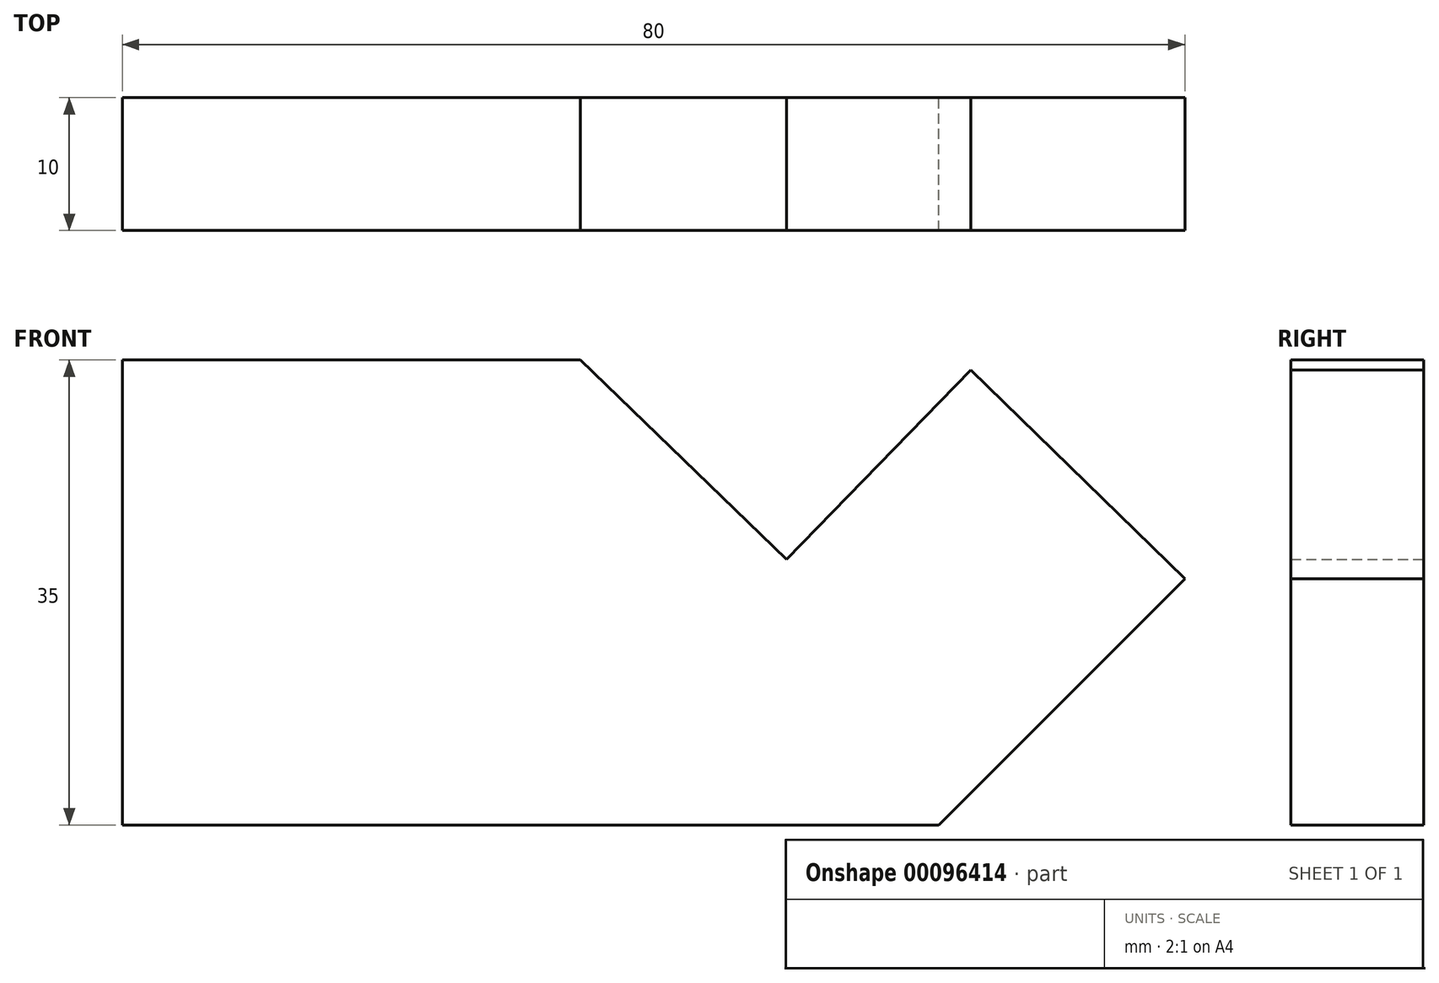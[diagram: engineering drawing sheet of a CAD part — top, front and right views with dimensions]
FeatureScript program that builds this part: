
annotation { "Feature Type Name" : "Feature", "Feature Type Description" : "" }
export const myFeature = defineFeature(function(context is Context, id is Id, definition is map)
    precondition{}
    {
        {
            var Q0;
            Q0=qCreatedBy(makeId("Front.planeOp"),FACE);
            var sketch = newSketch(context, id + "F0", { "sketchPlane" : qUnion([Q0])});
            skLineSegment(sketch, "E0", {"start": v(0, 0) * mm, "end": v(0, 35) * mm});
            skLineSegment(sketch, "E1", {"start": v(0, 35) * mm, "end": v(34.47, 35) * mm});
            skLineSegment(sketch, "E2", {"start": v(34.47, 35) * mm, "end": v(50, 20) * mm});
            skLineSegment(sketch, "E3", {"start": v(50, 20) * mm, "end": v(63.9, 34.25) * mm});
            skLineSegment(sketch, "E4", {"start": v(61.48, 0) * mm, "end": v(0, 0) * mm});
            skLineSegment(sketch, "E5", {"start": v(61.48, 0) * mm, "end": v(80, 18.52) * mm});
            skLineSegment(sketch, "E6", {"start": v(80, 18.52) * mm, "end": v(63.9, 34.25) * mm});
            skSolve(sketch);
        }
        {
            var Q0;
            Q0=makeQuery(id+"F0.imprint","IMPRINT",FACE,{"disambiguationData":[TD([[makeQuery(id+"F0.imprint","IMPRINT",EDGE,{"derivedFrom":sQuery(id+"F0.wireOp",EDGE,"E0")}),-1.0]])]});
            var Q1;
            Q1=makeQuery(id+"F0.imprint","IMPRINT",FACE,{"disambiguationData":[TD([[makeQuery(id+"F0.imprint","IMPRINT",EDGE,{"derivedFrom":sQuery(id+"F0.wireOp",EDGE,"E0")}),-1.0]])]});
            extrude(context, id + "F1", {"entities" : qUnion([Q0, Q1]), "depth" : 10 * mm});
        }
    });
